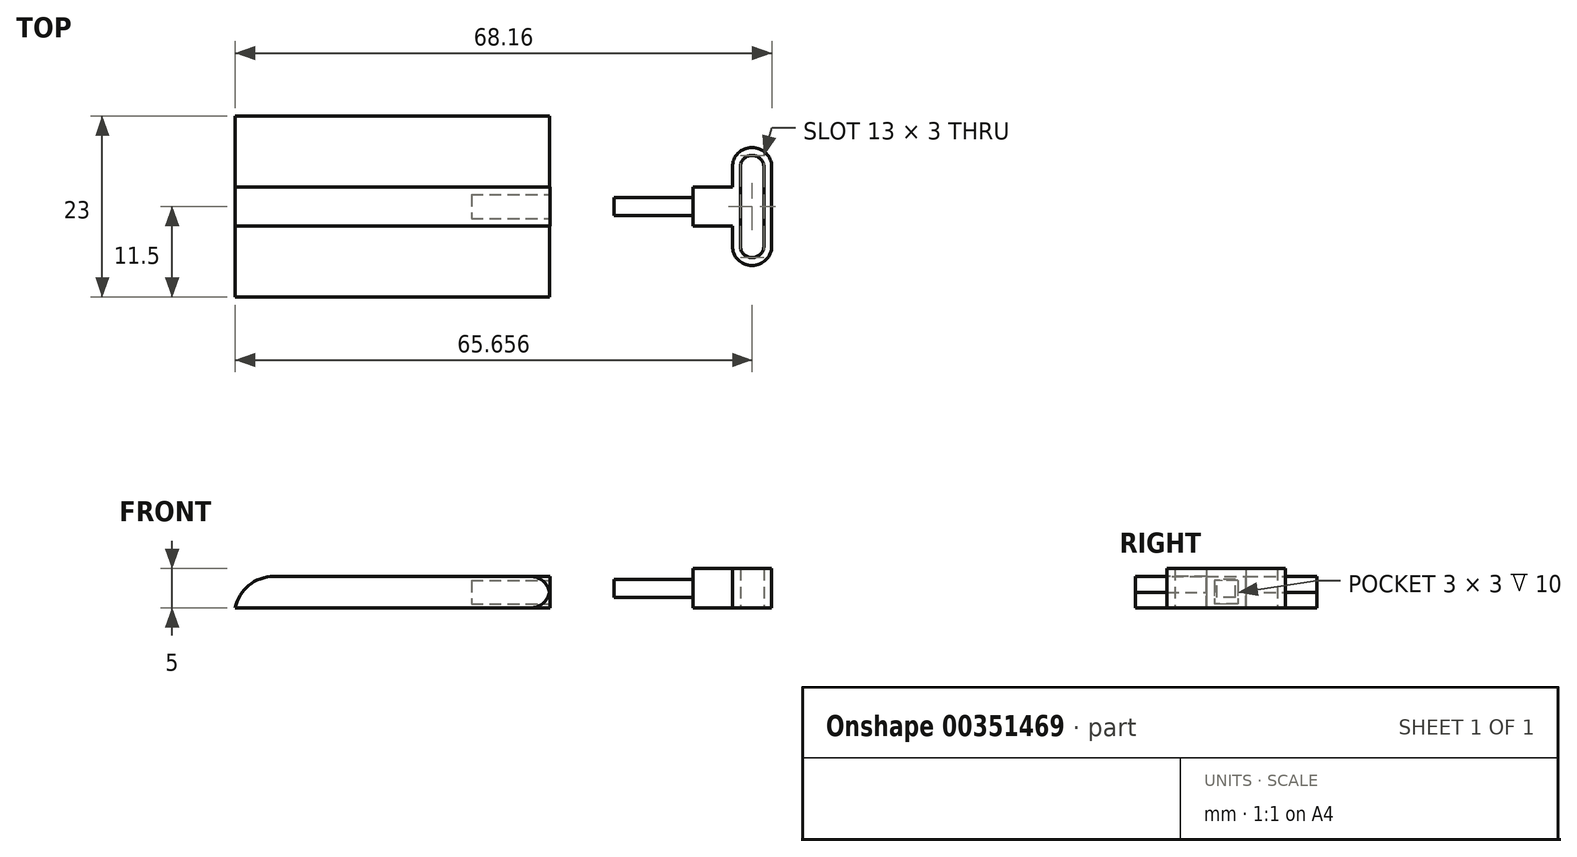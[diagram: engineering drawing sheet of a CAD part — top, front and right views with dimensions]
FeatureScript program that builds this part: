
annotation { "Feature Type Name" : "Feature", "Feature Type Description" : "" }
export const myFeature = defineFeature(function(context is Context, id is Id, definition is map)
    precondition{}
    {
        {
            var Q0;
            Q0=qCreatedBy(makeId("Right.planeOp"),FACE);
            var sketch = newSketch(context, id + "F0", { "sketchPlane" : qUnion([Q0])});
            skLineSegment(sketch, "E0.bottom", {"start": v(0, 0) * mm, "end": v(5, 0) * mm});
            skLineSegment(sketch, "E0.top", {"start": v(0, 4) * mm, "end": v(5, 4) * mm});
            skLineSegment(sketch, "E0.left", {"start": v(0, 0) * mm, "end": v(0, 4) * mm});
            skLineSegment(sketch, "E0.right", {"start": v(5, 0) * mm, "end": v(5, 4) * mm});
            skLineSegment(sketch, "E1.bottom", {"start": v(5, 4) * mm, "end": v(14, 4) * mm});
            skLineSegment(sketch, "E1.top", {"start": v(5, 0) * mm, "end": v(14, 0) * mm});
            skLineSegment(sketch, "E1.left", {"start": v(5, 4) * mm, "end": v(5, 0) * mm});
            skLineSegment(sketch, "E1.right", {"start": v(14, 4) * mm, "end": v(14, 0) * mm});
            skLineSegment(sketch, "E2.bottom", {"start": v(0, 4) * mm, "end": v(-9, 4) * mm});
            skLineSegment(sketch, "E2.top", {"start": v(0, 0) * mm, "end": v(-9, 0) * mm});
            skLineSegment(sketch, "E2.left", {"start": v(0, 4) * mm, "end": v(0, 0) * mm});
            skLineSegment(sketch, "E2.right", {"start": v(-9, 4) * mm, "end": v(-9, 0) * mm});
            skSolve(sketch);
        }
        {
            var Q0;
            Q0=makeQuery(id+"F0.imprint","IMPRINT",FACE,{"disambiguationData":[TD([[makeQuery(id+"F0.imprint","IMPRINT",EDGE,{"derivedFrom":sQuery(id+"F0.wireOp",EDGE,"E2.bottom")}),1.0]])]});
            var Q1;
            Q1=makeQuery(id+"F0.imprint","IMPRINT",FACE,{"disambiguationData":[TD([[makeQuery(id+"F0.imprint","IMPRINT",EDGE,{"derivedFrom":sQuery(id+"F0.wireOp",EDGE,"E1.bottom")}),-1.0]])]});
            extrude(context, id + "F1", {"entities" : qUnion([Q0, Q1]), "depth" : 40 * mm});
        }
        {
            var Q0;
            Q0=makeQuery(id+"F0.imprint","IMPRINT",FACE,{"disambiguationData":[TD([[makeQuery(id+"F0.imprint","IMPRINT",EDGE,{"derivedFrom":sQuery(id+"F0.wireOp",EDGE,"E0.bottom")}),1.0]])]});
            extrude(context, id + "F2", {"entities" : qUnion([Q0]), "depth" : 40 * mm});
        }
        {
            var Q0;
            Q0=makeQuery(id+"F2.opExtrude","CAP_FACE",FACE,{"disambiguationData":[OSD([sQuery(id+"F0.wireOp",EDGE,"E0.bottom"),sQuery(id+"F0.wireOp",EDGE,"E0.top"),sQuery(id+"F0.wireOp",EDGE,"E1.left"),sQuery(id+"F0.wireOp",EDGE,"E2.left")])],"isStart":false});
            var sketch = newSketch(context, id + "F3", { "sketchPlane" : qUnion([Q0])});
            skLineSegment(sketch, "E3", {"start": v(2.5, 4) * mm, "end": v(2.5, 0) * mm, "construction": true});
            skLineSegment(sketch, "E4", {"start": v(2.5, 0) * mm, "end": v(0, 2) * mm, "construction": true});
            skLineSegment(sketch, "E5", {"start": v(0, 2) * mm, "end": v(5, 2) * mm, "construction": true});
            skLineSegment(sketch, "E6.bottom", {"start": v(4, 3.5) * mm, "end": v(1, 3.5) * mm});
            skLineSegment(sketch, "E6.top", {"start": v(4, 0.5) * mm, "end": v(1, 0.5) * mm});
            skLineSegment(sketch, "E6.left", {"start": v(4, 3.5) * mm, "end": v(4, 0.5) * mm});
            skLineSegment(sketch, "E6.right", {"start": v(1, 3.5) * mm, "end": v(1, 0.5) * mm});
            skPoint(sketch, "E6.middle", {"position": v(2.5, 2) * mm});
            skSolve(sketch);
        }
        {
            var Q0;
            Q0 = qSketchRegion(id + "F3", true);
            extrude(context, id + "F4", {"entities" : qUnion([Q0]), "operationType" : NewBodyOperationType.REMOVE, "oppositeDirection" : true, "depth" : 10 * mm});
        }
        {
            var Q0;
            Q0=makeQuery(id+"F1.opExtrude","CAP_EDGE",EDGE,{"disambiguationData":[OSD([sQuery(id+"F0.wireOp",EDGE,"E2.bottom")])],"isStart":true});
            var Q1;
            Q1=makeQuery(id+"F2.opExtrude","CAP_EDGE",EDGE,{"disambiguationData":[OSD([sQuery(id+"F0.wireOp",EDGE,"E0.top")])],"isStart":true});
            var Q2;
            Q2=makeQuery(id+"F1.opExtrude","CAP_EDGE",EDGE,{"disambiguationData":[OSD([sQuery(id+"F0.wireOp",EDGE,"E1.bottom")])],"isStart":true});
            fillet(context, id + "F5", {"entities" : qUnion([Q0, Q1, Q2]), "radius" : 5 * mm, "tangentPropagation" : true, "allowEdgeOverflow" : false});
        }
        {
            var Q0;
            Q0=makeQuery(id+"F1.opExtrude","CAP_EDGE",EDGE,{"disambiguationData":[OSD([sQuery(id+"F0.wireOp",EDGE,"E1.bottom")])],"isStart":false});
            var Q1;
            Q1=makeQuery(id+"F1.opExtrude","CAP_EDGE",EDGE,{"disambiguationData":[OSD([sQuery(id+"F0.wireOp",EDGE,"E1.top")])],"isStart":false});
            var Q2;
            Q2=makeQuery(id+"F1.opExtrude","CAP_EDGE",EDGE,{"disambiguationData":[OSD([sQuery(id+"F0.wireOp",EDGE,"E2.bottom")])],"isStart":false});
            var Q3;
            Q3=makeQuery(id+"F1.opExtrude","CAP_EDGE",EDGE,{"disambiguationData":[OSD([sQuery(id+"F0.wireOp",EDGE,"E2.top")])],"isStart":false});
            fillet(context, id + "F6", {"entities" : qUnion([Q0, Q1, Q2, Q3]), "radius" : 2.5 * mm, "tangentPropagation" : true, "allowEdgeOverflow" : false});
        }
        {
            var Q0;
            Q0=qCreatedBy(makeId("Top.planeOp"),FACE);
            var sketch = newSketch(context, id + "F7", { "sketchPlane" : qUnion([Q0])});
            skLineSegment(sketch, "E7", {"start": v(58.16, 0) * mm, "end": v(58.16, 5) * mm});
            skLineSegment(sketch, "E8", {"start": v(58.16, 5) * mm, "end": v(63.16, 5) * mm});
            skLineSegment(sketch, "E9", {"start": v(63.16, 5) * mm, "end": v(63.16, 10) * mm});
            skLineSegment(sketch, "E10", {"start": v(63.16, 10) * mm, "end": v(68.16, 10) * mm});
            skLineSegment(sketch, "E11", {"start": v(68.16, 10) * mm, "end": v(68.16, -5) * mm});
            skLineSegment(sketch, "E12", {"start": v(68.16, -5) * mm, "end": v(63.16, -5) * mm});
            skLineSegment(sketch, "E13", {"start": v(63.16, -5) * mm, "end": v(63.16, 0) * mm});
            skLineSegment(sketch, "E14", {"start": v(63.16, 0) * mm, "end": v(58.16, 0) * mm});
            skLineSegment(sketch, "E15", {"start": v(65.66, 10) * mm, "end": v(65.66, -5) * mm, "construction": true});
            skLineSegment(sketch, "E16", {"start": v(65.66, -5) * mm, "end": v(63.16, -2.5) * mm, "construction": true});
            skLineSegment(sketch, "E17", {"start": v(63.16, -2.5) * mm, "end": v(68.16, -2.5) * mm});
            skLineSegment(sketch, "E18", {"start": v(63.16, 7.5) * mm, "end": v(68.16, 7.5) * mm});
            skPoint(sketch, "E19", {"position": v(65.66, 7.5) * mm});
            skPoint(sketch, "E20", {"position": v(65.66, -2.5) * mm});
            skLineSegment(sketch, "E21", {"start": v(65.66, 7.5) * mm, "end": v(67.16, 7.5) * mm, "construction": true});
            skLineSegment(sketch, "E22", {"start": v(67.16, 7.5) * mm, "end": v(67.16, -2.5) * mm});
            skLineSegment(sketch, "E23", {"start": v(65.66, -2.5) * mm, "end": v(64.16, -2.5) * mm, "construction": true});
            skLineSegment(sketch, "E24", {"start": v(64.16, -2.5) * mm, "end": v(64.16, 7.5) * mm});
            skLineSegment(sketch, "E25", {"start": v(64.16, 7.5) * mm, "end": v(65.66, 7.5) * mm, "construction": true});
            skSolve(sketch);
        }
        {
            var Q0;
            Q0 = qSketchRegion(id + "F7", true);
            extrude(context, id + "F8", {"entities" : qUnion([Q0]), "depth" : 5 * mm});
        }
        {
            var Q0;
            Q0=sQuery(id+"F7.wireOp",VERTEX,"E19");
            var Q1;
            Q1=sQuery(id+"F7.wireOp",VERTEX,"E20");
            var Q2;
            Q2=makeQuery(id+"F8.opExtrude","SWEPT_BODY",BODY,{"disambiguationData":[OSD([sQuery(id+"F7.wireOp",EDGE,"E7"),sQuery(id+"F7.wireOp",EDGE,"E8"),sQuery(id+"F7.wireOp",EDGE,"E9"),sQuery(id+"F7.wireOp",EDGE,"E10"),sQuery(id+"F7.wireOp",EDGE,"E11"),sQuery(id+"F7.wireOp",EDGE,"E12"),sQuery(id+"F7.wireOp",EDGE,"E13"),sQuery(id+"F7.wireOp",EDGE,"E14")])]});
            hole(context, id + "F9", {"style" : HoleStyle.SIMPLE, "endStyle" : HoleEndStyle.THROUGH, "oppositeDirection" : true, "holeDiameter" : 3 * mm, "isTappedThrough" : true, "tappedDepth" : 12 * mm, "tapClearance" : 3, "locations" : qUnion([Q0, Q1]), "scope" : qUnion([Q2])});
        }
        {
            var Q0;
            Q0=makeQuery(id+"F8.opExtrude","SWEPT_FACE",FACE,{"disambiguationData":[OSD([sQuery(id+"F7.wireOp",EDGE,"E7")])]});
            var sketch = newSketch(context, id + "F10", { "sketchPlane" : qUnion([Q0])});
            skLineSegment(sketch, "E26", {"start": v(-2.5, 0) * mm, "end": v(-2.5, 5) * mm, "construction": true});
            skLineSegment(sketch, "E27", {"start": v(-2.5, 5) * mm, "end": v(0, 2.5) * mm, "construction": true});
            skLineSegment(sketch, "E28", {"start": v(0, 2.5) * mm, "end": v(-5, 2.5) * mm, "construction": true});
            skLineSegment(sketch, "E29.bottom", {"start": v(-3.65, 1.35) * mm, "end": v(-1.35, 1.35) * mm});
            skLineSegment(sketch, "E29.top", {"start": v(-3.65, 3.65) * mm, "end": v(-1.35, 3.65) * mm});
            skLineSegment(sketch, "E29.left", {"start": v(-3.65, 1.35) * mm, "end": v(-3.65, 3.65) * mm});
            skLineSegment(sketch, "E29.right", {"start": v(-1.35, 1.35) * mm, "end": v(-1.35, 3.65) * mm});
            skPoint(sketch, "E29.middle", {"position": v(-2.5, 2.5) * mm});
            skSolve(sketch);
        }
        {
            var Q0;
            Q0=makeQuery(id+"F10.imprint","IMPRINT",FACE,{"disambiguationData":[TD([[makeQuery(id+"F10.imprint","IMPRINT",EDGE,{"derivedFrom":sQuery(id+"F10.wireOp",EDGE,"E29.bottom")}),1.0]])]});
            extrude(context, id + "F11", {"entities" : qUnion([Q0]), "operationType" : NewBodyOperationType.ADD, "depth" : 10 * mm});
        }
        {
            var Q0;
            Q0=makeQuery(id+"F8.opExtrude","SWEPT_EDGE",EDGE,{"disambiguationData":[OSD([sQuery(id+"F7.wireOp",EDGE,"E10"),sQuery(id+"F7.wireOp",EDGE,"E11")])]});
            var Q1;
            Q1=makeQuery(id+"F8.opExtrude","SWEPT_EDGE",EDGE,{"disambiguationData":[OSD([sQuery(id+"F7.wireOp",EDGE,"E9"),sQuery(id+"F7.wireOp",EDGE,"E10")])]});
            var Q2;
            Q2=makeQuery(id+"F8.opExtrude","SWEPT_EDGE",EDGE,{"disambiguationData":[OSD([sQuery(id+"F7.wireOp",EDGE,"E11"),sQuery(id+"F7.wireOp",EDGE,"E12")])]});
            var Q3;
            Q3=makeQuery(id+"F8.opExtrude","SWEPT_EDGE",EDGE,{"disambiguationData":[OSD([sQuery(id+"F7.wireOp",EDGE,"E12"),sQuery(id+"F7.wireOp",EDGE,"E13")])]});
            fillet(context, id + "F12", {"entities" : qUnion([Q0, Q1, Q2, Q3]), "radius" : 2.5 * mm, "tangentPropagation" : true, "allowEdgeOverflow" : false});
        }
    });
